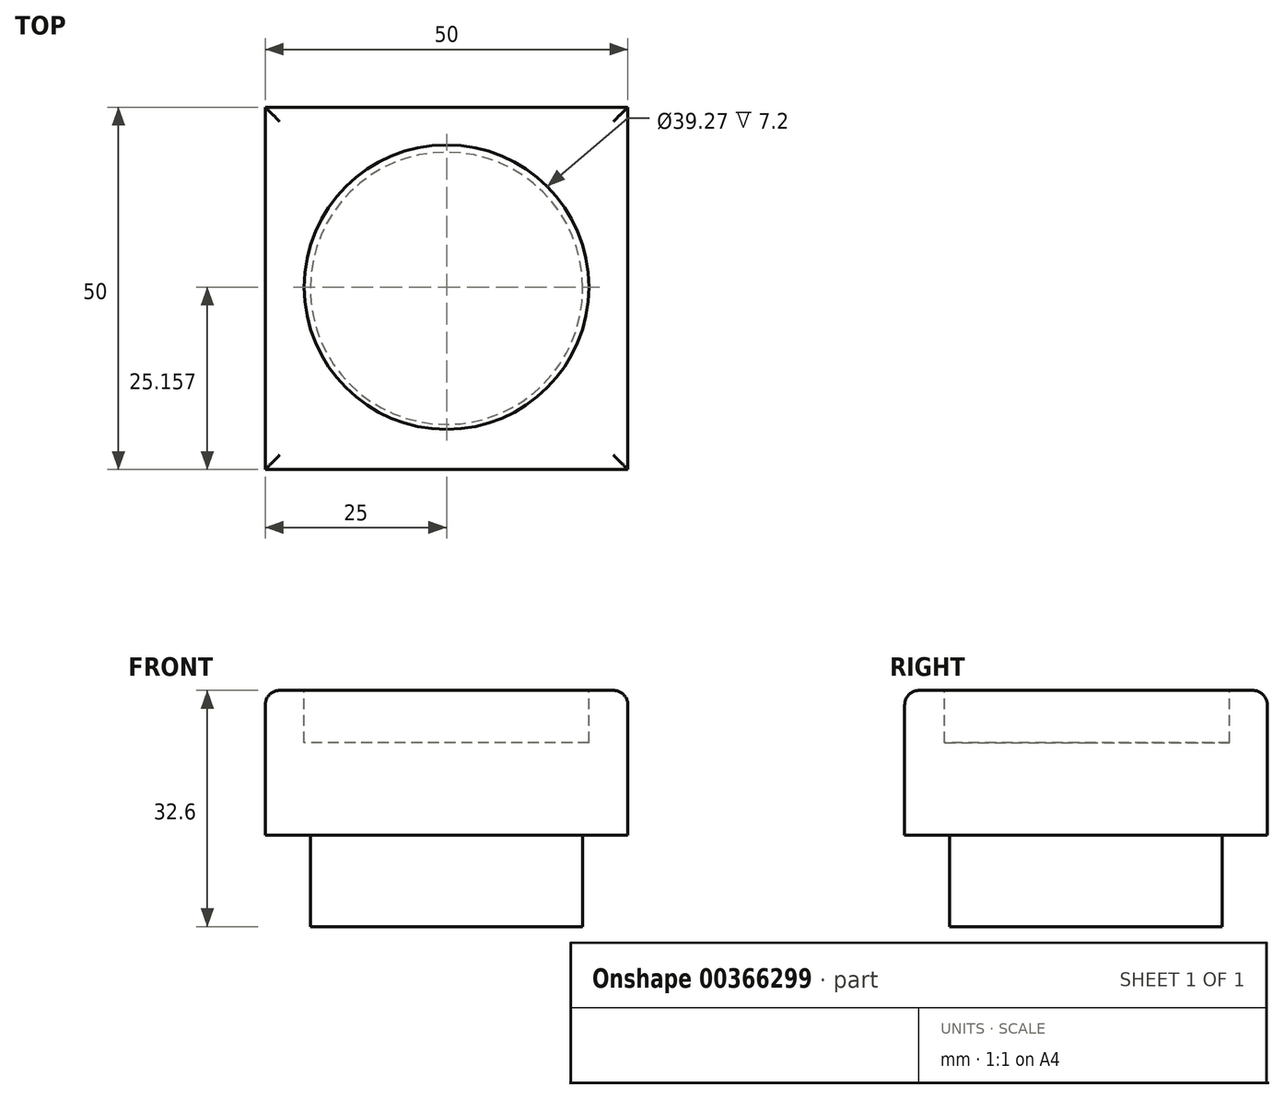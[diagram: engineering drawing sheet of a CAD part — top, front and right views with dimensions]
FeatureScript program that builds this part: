
annotation { "Feature Type Name" : "Feature", "Feature Type Description" : "" }
export const myFeature = defineFeature(function(context is Context, id is Id, definition is map)
    precondition{}
    {
        {
            var Q0;
            Q0=qCreatedBy(makeId("Top.planeOp"),FACE);
            var sketch = newSketch(context, id + "F0", { "sketchPlane" : qUnion([Q0])});
            skLineSegment(sketch, "E0.bottom", {"start": v(0, 0) * mm, "end": v(50, 0) * mm});
            skLineSegment(sketch, "E0.top", {"start": v(0, 50) * mm, "end": v(50, 50) * mm});
            skLineSegment(sketch, "E0.left", {"start": v(0, 0) * mm, "end": v(0, 50) * mm});
            skLineSegment(sketch, "E0.right", {"start": v(50, 0) * mm, "end": v(50, 50) * mm});
            skSolve(sketch);
        }
        {
            var Q0;
            Q0=makeQuery(id+"F0.imprint","IMPRINT",FACE,{"disambiguationData":[TD([[makeQuery(id+"F0.imprint","IMPRINT",EDGE,{"derivedFrom":sQuery(id+"F0.wireOp",EDGE,"E0.bottom")}),1.0]])]});
            extrude(context, id + "F1", {"entities" : qUnion([Q0]), "depth" : 20 * mm});
        }
        {
            var Q0;
            Q0=makeQuery(id+"F1.opExtrude","CAP_EDGE",EDGE,{"disambiguationData":[OSD([sQuery(id+"F0.wireOp",EDGE,"E0.right")])],"isStart":false});
            var Q1;
            Q1=makeQuery(id+"F1.opExtrude","CAP_EDGE",EDGE,{"disambiguationData":[OSD([sQuery(id+"F0.wireOp",EDGE,"E0.top")])],"isStart":false});
            var Q2;
            Q2=makeQuery(id+"F1.opExtrude","CAP_EDGE",EDGE,{"disambiguationData":[OSD([sQuery(id+"F0.wireOp",EDGE,"E0.left")])],"isStart":false});
            var Q3;
            Q3=makeQuery(id+"F1.opExtrude","CAP_EDGE",EDGE,{"disambiguationData":[OSD([sQuery(id+"F0.wireOp",EDGE,"E0.bottom")])],"isStart":false});
            fillet(context, id + "F2", {"entities" : qUnion([Q0, Q1, Q2, Q3]), "radius" : 2 * mm, "tangentPropagation" : true, "allowEdgeOverflow" : false});
        }
        {
            var Q0;
            Q0=makeQuery(id+"F1.opExtrude","CAP_FACE",FACE,{"disambiguationData":[OSD([sQuery(id+"F0.wireOp",EDGE,"E0.bottom"),sQuery(id+"F0.wireOp",EDGE,"E0.top"),sQuery(id+"F0.wireOp",EDGE,"E0.left"),sQuery(id+"F0.wireOp",EDGE,"E0.right")])],"isStart":false});
            var sketch = newSketch(context, id + "F3", { "sketchPlane" : qUnion([Q0])});
            skLineSegment(sketch, "E1", {"start": v(2, 25) * mm, "end": v(48, 25) * mm, "construction": true});
            skCircle(sketch, "E2", {"center": v(25, 25) * mm, "radius": 18.8 * mm});
            skSolve(sketch);
        }
        {
            var Q0;
            Q0=makeQuery(id+"F3.imprint","IMPRINT",FACE,{"disambiguationData":[TD([[makeQuery(id+"F3.imprint","IMPRINT",EDGE,{"derivedFrom":sQuery(id+"F3.wireOp",EDGE,"E2")}),1.0]])]});
            extrude(context, id + "F4", {"entities" : qUnion([Q0]), "operationType" : NewBodyOperationType.ADD, "oppositeDirection" : true, "depth" : 32.6 * mm});
        }
        {
            var Q0;
            Q0=makeQuery(id+"F1.opExtrude","CAP_FACE",FACE,{"disambiguationData":[OSD([sQuery(id+"F0.wireOp",EDGE,"E0.bottom"),sQuery(id+"F0.wireOp",EDGE,"E0.top"),sQuery(id+"F0.wireOp",EDGE,"E0.left"),sQuery(id+"F0.wireOp",EDGE,"E0.right")])],"isStart":false});
            var sketch = newSketch(context, id + "F5", { "sketchPlane" : qUnion([Q0])});
            skSolve(sketch);
        }
        {
            var Q0;
            {var subQ0=sQuery(id+"F0.wireOp",EDGE,"E0.right");var subQ1=sQuery(id+"F0.wireOp",EDGE,"E0.left");var subQ2=sQuery(id+"F0.wireOp",EDGE,"E0.top");var subQ3=sQuery(id+"F0.wireOp",EDGE,"E0.bottom");var subQ4=makeQuery(id+"F1.opExtrude","CAP_FACE",FACE,{"disambiguationData":[OSD([subQ3,subQ2,subQ1,subQ0])],"isStart":false});Q0=makeQuery(id+"F5.imprint","IMPRINT",FACE,{"disambiguationData":[TD([[makeQuery(id+"F5.imprint","IMPRINT",EDGE,{"derivedFrom":makeQuery(id+"F2.opFillet","BLEND_EDGE",EDGE,{"blendedFrom":[makeQuery(id+"F1.opExtrude","CAP_EDGE",EDGE,{"disambiguationData":[OSD([subQ3])],"isStart":false}),subQ4],"blendedInto":[subQ4]})}),1.0]])]});}
            var sketch = newSketch(context, id + "F6", { "sketchPlane" : qUnion([Q0])});
            skLineSegment(sketch, "E3.0.0", {"start": v(48, 48) * mm, "end": v(2, 48) * mm});
            skLineSegment(sketch, "E3.0.1", {"start": v(2, 48) * mm, "end": v(2, 2) * mm});
            skLineSegment(sketch, "E3.0.2", {"start": v(2, 2) * mm, "end": v(48, 2) * mm});
            skLineSegment(sketch, "E3.0.3", {"start": v(48, 2) * mm, "end": v(48, 48) * mm});
            skCircle(sketch, "E4", {"center": v(25, 25.16) * mm, "radius": 19.64 * mm});
            skLineSegment(sketch, "E5", {"start": v(25, 48) * mm, "end": v(25, 25.16) * mm, "construction": true});
            skSolve(sketch);
        }
        {
            var Q0;
            Q0=makeQuery(id+"F6.imprint","IMPRINT",FACE,{"disambiguationData":[TD([[makeQuery(id+"F6.imprint","IMPRINT",EDGE,{"derivedFrom":sQuery(id+"F6.wireOp",EDGE,"E4")}),1.0]])]});
            extrude(context, id + "F7", {"entities" : qUnion([Q0]), "operationType" : NewBodyOperationType.REMOVE, "oppositeDirection" : true, "depth" : 7.2 * mm});
        }
    });
